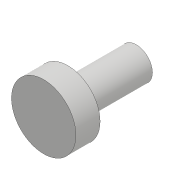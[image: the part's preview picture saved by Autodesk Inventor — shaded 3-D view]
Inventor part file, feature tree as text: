
AUTODESK INVENTOR PART (.ipt)
format: ipt  version: 2018 (Build 220112000, 112)  size: 92,160 bytes
history: native  units: mm
features: sketch x3, extrude x2, hole x1
ambient origin geometry x8: Origin, YZ Plane, XZ Plane, XY Plane, X Axis, Y Axis, Z Axis, Center Point
bodies: Solid1 (feature_tree)
feature tree (6):
  extrude  "Extrusion1"  Depth=3.0mm TaperAngle=0.0deg
  extrude  "Extrusion2"  Depth=8.5mm TaperAngle=0.0deg
  hole  "Hole1"  [1 undecoded]
  sketch  "Sketch1"  dims[d0=8.0mm d1=3.0mm d2=0.0mm]
  sketch  "Sketch2"  dims[d3=4.0mm d4=8.5mm d5=0.0mm]
  sketch  "Sketch3"  dims[d6=3.1mm d7=6.0mm d8=6.3mm d9=2.0mm d10=90.0deg d11=8.0mm d12=20.594885mm]
note: 1 required parameter value undecoded (feature->parameter linkage not recoverable at this tier; creation-order binding heuristic only, values carry confidence <= 0.55)
